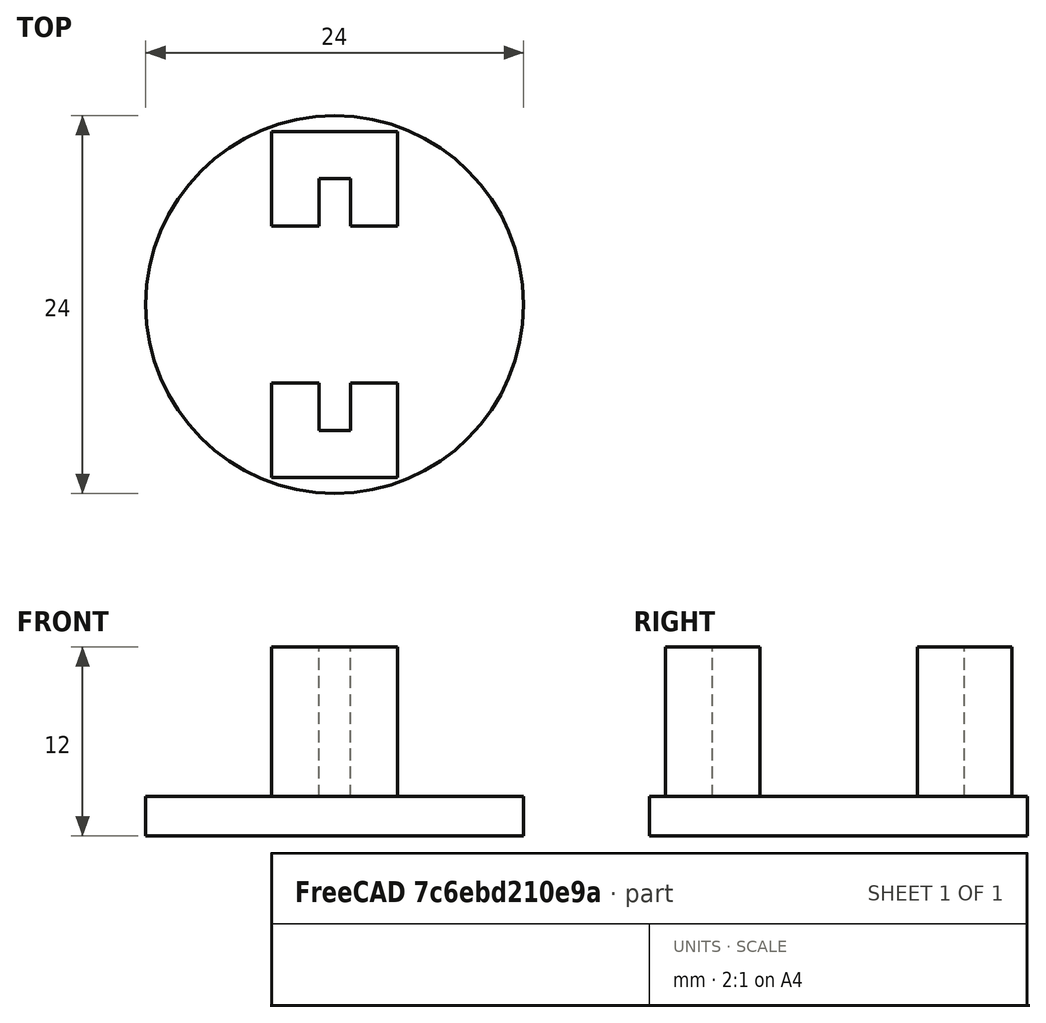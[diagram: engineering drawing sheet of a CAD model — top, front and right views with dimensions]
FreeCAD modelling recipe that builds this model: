
FCSTD DOCUMENT  (FreeCAD 0.16R6710 (Git))
Label: pie-semaforo
License: All rights reserved
LicenseURL: http://en.wikipedia.org/wiki/All_rights_reserved
objects: Part::Box×3, Part::MultiFuse×2, Part::Cylinder×1, Part::Cut×1
note: 7 computed .brp shape members not serialized (recipe doc carries the construction recipe); baked Part::Feature solids carry a one-line shape summary decoded from their .brp

FEATURE [Part::Cylinder] Cylinder
  Angle = 360
  Height = 2.5
  Radius = 12
FEATURE [Part::Box] Box  label="Cube"
  Height = 10
  Length = 8
  Placement = pos=(-4,-11,2) rot=(0,0,1;0rad)
  Width = 22
FEATURE [Part::Box] Box001  label="Cube001"
  Height = 10
  Length = 2
  Placement = pos=(-1,-8,2) rot=(0,0,1;0rad)
  Width = 16
FEATURE [Part::Box] Box002  label="Cube002"
  Height = 10
  Length = 10
  Placement = pos=(-5,-5,2) rot=(0,0,1;0rad)
  Width = 10
FEATURE [Part::MultiFuse] Fusion
  Shapes = -> [Box001,Box002]
FEATURE [Part::Cut] Cut
  Base = -> Box
  Tool = -> Fusion
FEATURE [Part::MultiFuse] Fusion001
  Shapes = -> [Cut,Cylinder]
